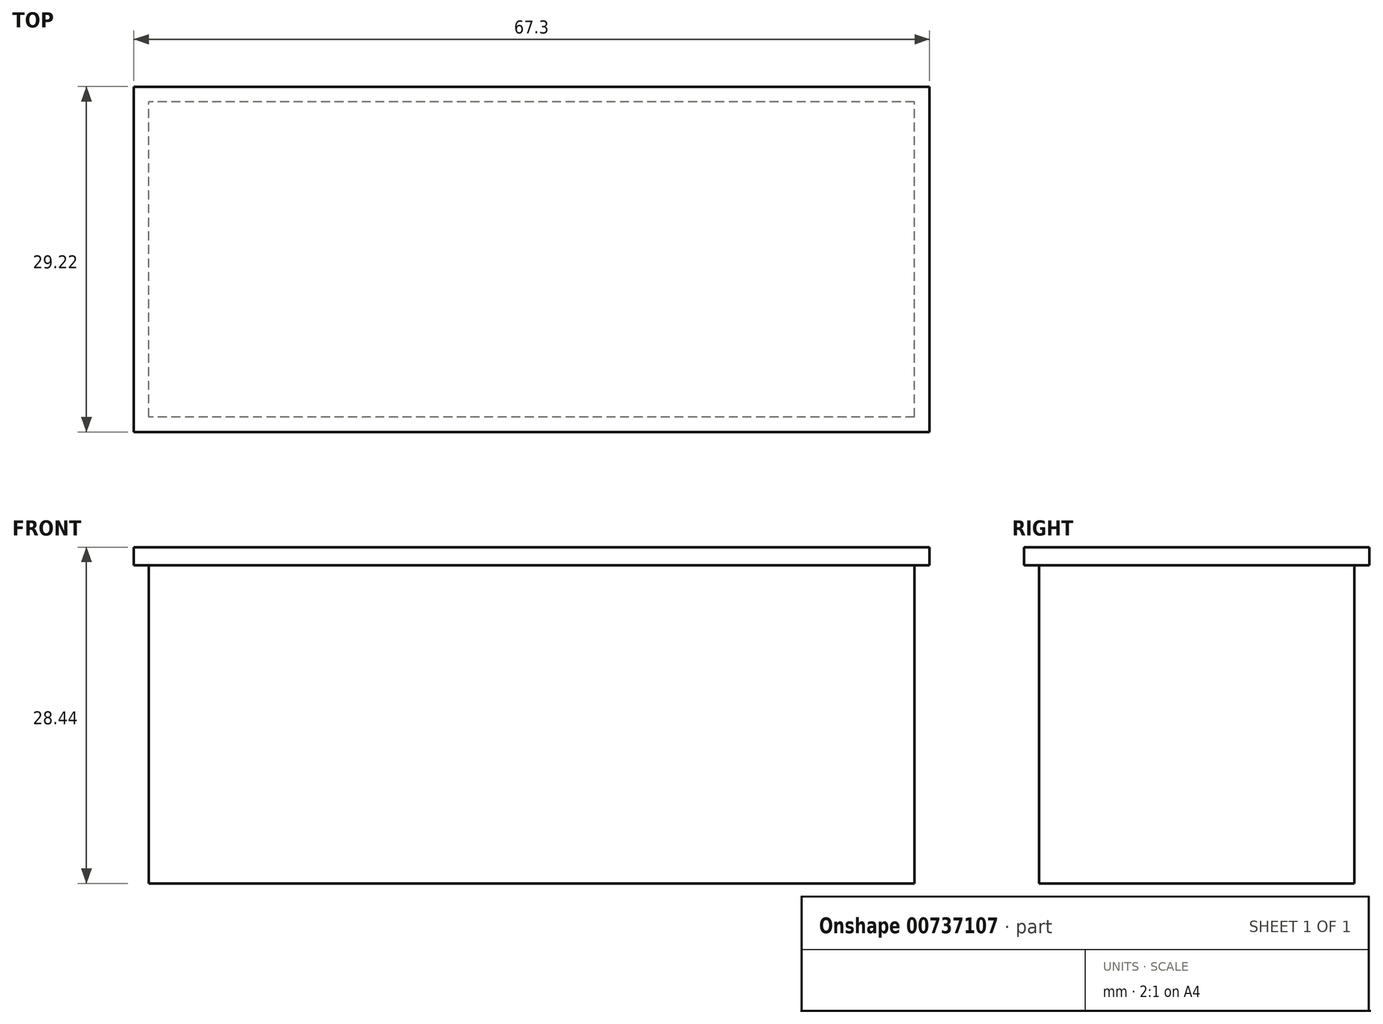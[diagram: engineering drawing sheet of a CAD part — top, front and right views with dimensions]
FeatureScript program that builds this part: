
annotation { "Feature Type Name" : "Feature", "Feature Type Description" : "" }
export const myFeature = defineFeature(function(context is Context, id is Id, definition is map)
    precondition{}
    {
        {
            var Q0;
            Q0=qCreatedBy(makeId("Top.planeOp"),FACE);
            var sketch = newSketch(context, id + "F0", { "sketchPlane" : qUnion([Q0])});
            skLineSegment(sketch, "E0.bottom", {"start": v(33.66, -14.6) * mm, "end": v(-33.66, -14.6) * mm});
            skLineSegment(sketch, "E0.top", {"start": v(33.66, 14.6) * mm, "end": v(-33.66, 14.6) * mm});
            skLineSegment(sketch, "E0.left", {"start": v(33.66, -14.6) * mm, "end": v(33.66, 14.6) * mm});
            skLineSegment(sketch, "E0.right", {"start": v(-33.66, -14.6) * mm, "end": v(-33.66, 14.6) * mm});
            skPoint(sketch, "E0.middle", {"position": v(0, 0) * mm});
            skSolve(sketch);
        }
        {
            var Q0;
            Q0 = qSketchRegion(id + "F0", true);
            extrude(context, id + "F1", {"entities" : qUnion([Q0]), "depth" : 1.52 * mm, "offsetDistance" : 25.4 * mm});
        }
        {
            var Q0;
            Q0=makeQuery(id+"F1.opExtrude","CAP_FACE",FACE,{"disambiguationData":[OSD([sQuery(id+"F0.wireOp",EDGE,"E0.bottom"),sQuery(id+"F0.wireOp",EDGE,"E0.top"),sQuery(id+"F0.wireOp",EDGE,"E0.left"),sQuery(id+"F0.wireOp",EDGE,"E0.right")])],"isStart":true});
            var sketch = newSketch(context, id + "F2", { "sketchPlane" : qUnion([Q0])});
            skLineSegment(sketch, "E1.bottom", {"start": v(32.39, 13.34) * mm, "end": v(-32.39, 13.34) * mm});
            skLineSegment(sketch, "E1.top", {"start": v(32.39, -13.34) * mm, "end": v(-32.39, -13.34) * mm});
            skLineSegment(sketch, "E1.left", {"start": v(32.39, 13.34) * mm, "end": v(32.39, -13.34) * mm});
            skLineSegment(sketch, "E1.right", {"start": v(-32.39, 13.34) * mm, "end": v(-32.39, -13.34) * mm});
            skPoint(sketch, "E1.middle", {"position": v(0, 0) * mm});
            skSolve(sketch);
        }
        {
            var Q0;
            Q0 = qSketchRegion(id + "F2", true);
            extrude(context, id + "F3", {"entities" : qUnion([Q0]), "operationType" : NewBodyOperationType.ADD, "depth" : 26.92 * mm, "offsetDistance" : 25.4 * mm});
        }
    });
